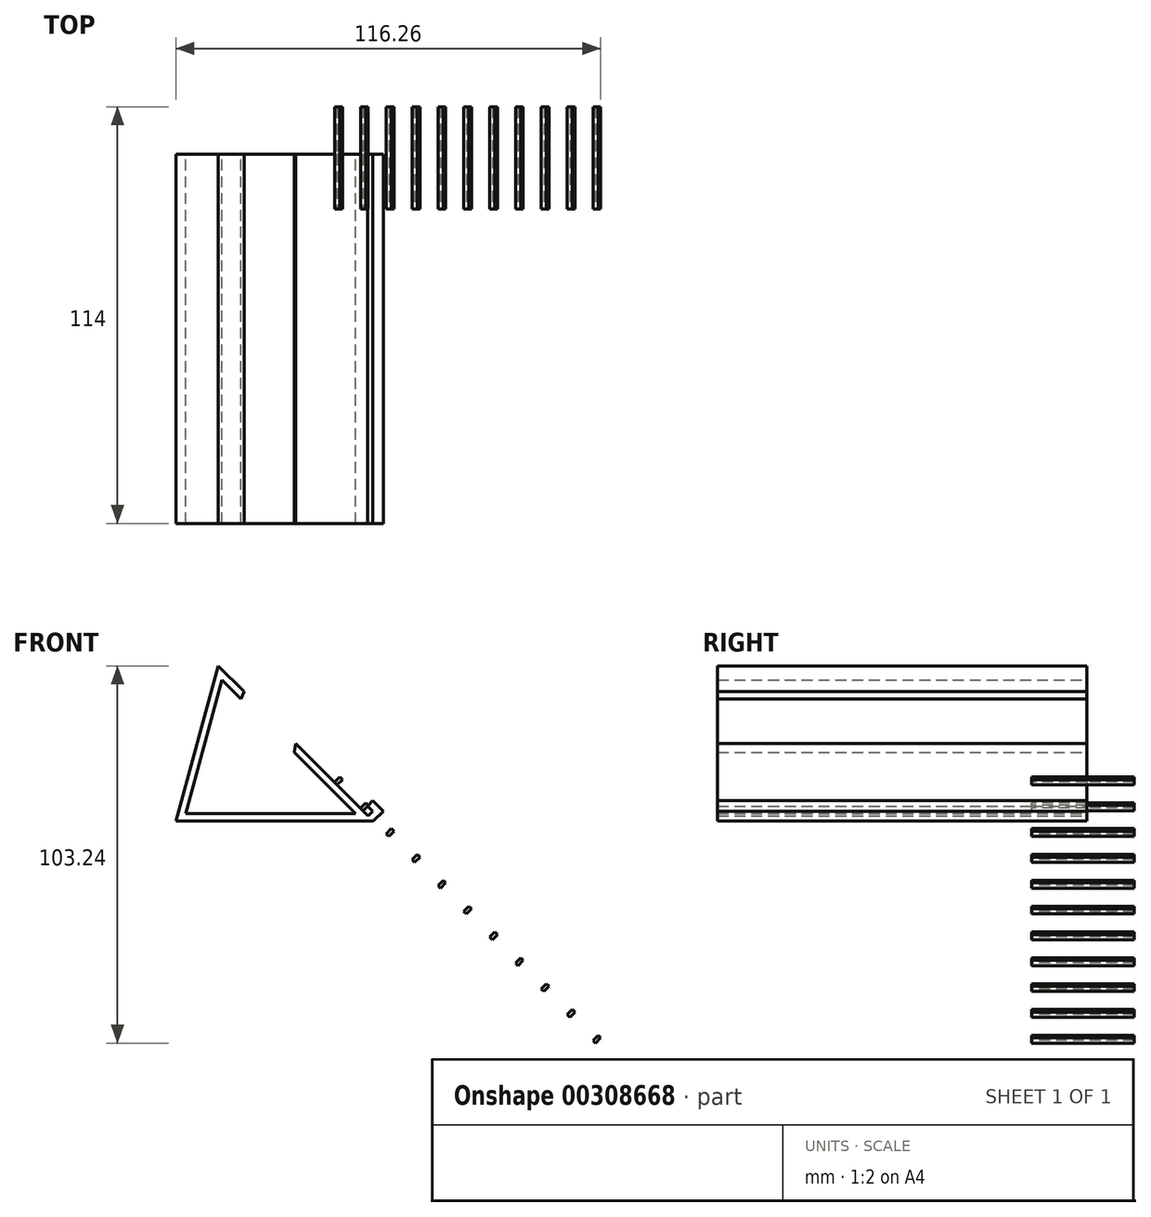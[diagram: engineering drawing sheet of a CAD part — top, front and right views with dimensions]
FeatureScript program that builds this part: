
annotation { "Feature Type Name" : "Feature", "Feature Type Description" : "" }
export const myFeature = defineFeature(function(context is Context, id is Id, definition is map)
    precondition{}
    {
        {
            var Q0;
            Q0=qCreatedBy(makeId("Front.planeOp"),FACE);
            var sketch = newSketch(context, id + "F0", { "sketchPlane" : qUnion([Q0])});
            skLineSegment(sketch, "E0", {"start": v(0, 21.21) * mm, "end": v(21.21, 0) * mm});
            skLineSegment(sketch, "E1", {"start": v(-9.71, 0) * mm, "end": v(21.21, 0) * mm});
            skLineSegment(sketch, "E2", {"start": v(0, 21.21) * mm, "end": v(-14.14, 35.36) * mm});
            skLineSegment(sketch, "E3", {"start": v(-32.82, 0) * mm, "end": v(-9.71, 0) * mm});
            skLineSegment(sketch, "E4", {"start": v(-14.14, 35.36) * mm, "end": v(-21.21, 42.43) * mm});
            skLineSegment(sketch, "E5", {"start": v(-21.21, 42.43) * mm, "end": v(-32.82, 0) * mm});
            skLineSegment(sketch, "E6", {"start": v(-20.2, 38.58) * mm, "end": v(-15.05, 33.44) * mm});
            skLineSegment(sketch, "E7", {"start": v(-15.05, 33.44) * mm, "end": v(-14.14, 35.36) * mm});
            skLineSegment(sketch, "E8", {"start": v(0, 21.21) * mm, "end": v(-0.44, 18.83) * mm});
            skLineSegment(sketch, "E9", {"start": v(-0.44, 18.83) * mm, "end": v(16.38, 2) * mm});
            skLineSegment(sketch, "E10", {"start": v(16.38, 2) * mm, "end": v(-30.2, 2) * mm});
            skLineSegment(sketch, "E11", {"start": v(-30.2, 2) * mm, "end": v(-20.2, 38.58) * mm});
            skLineSegment(sketch, "E12", {"start": v(21.21, 0) * mm, "end": v(23.9, 2.69) * mm});
            skLineSegment(sketch, "E13", {"start": v(23.9, 2.69) * mm, "end": v(21.07, 5.52) * mm});
            skLineSegment(sketch, "E14", {"start": v(21.07, 5.52) * mm, "end": v(19.66, 4.1) * mm});
            skLineSegment(sketch, "E15", {"start": v(19.66, 4.1) * mm, "end": v(21.07, 2.69) * mm});
            skLineSegment(sketch, "E16", {"start": v(21.07, 2.69) * mm, "end": v(19.8, 1.41) * mm});
            skSolve(sketch);
        }
        {
            var Q0;
            {var subQ3=sQuery(id+"F0.wireOp",EDGE,"E1");Q0=makeQuery(id+"F0.imprint","IMPRINT",FACE,{"disambiguationData":[TD([[makeQuery(id+"F0.imprint","IMPRINT",EDGE,{"derivedFrom":subQ3}),1.0]])]});}
            var Q1;
            {var subQ0=sQuery(id+"F0.wireOp",EDGE,"E12");Q1=makeQuery(id+"F0.imprint","IMPRINT",FACE,{"disambiguationData":[TD([[makeQuery(id+"F0.imprint","IMPRINT",EDGE,{"derivedFrom":subQ0}),1.0]])]});}
            extrude(context, id + "F1", {"entities" : qUnion([Q0, Q1]), "depth" : 101 * mm});
        }
        {
            var Q0;
            Q0=makeQuery(id+"F1.opExtrude","SWEPT_FACE",FACE,{"disambiguationData":[OSD([sQuery(id+"F0.wireOp",EDGE,"E0")])]});
            var sketch = newSketch(context, id + "F2", { "sketchPlane" : qUnion([Q0])});
            skLineSegment(sketch, "E17.bottom", {"start": v(13, -101) * mm, "end": v(-15, -101) * mm});
            skLineSegment(sketch, "E17.top", {"start": v(13, -100) * mm, "end": v(-15, -100) * mm});
            skLineSegment(sketch, "E17.left", {"start": v(13, -101) * mm, "end": v(13, -100) * mm});
            skLineSegment(sketch, "E17.right", {"start": v(-15, -101) * mm, "end": v(-15, -100) * mm});
            skLineSegment(sketch, "E18.bottom", {"start": v(13, -91) * mm, "end": v(-15, -91) * mm});
            skLineSegment(sketch, "E18.top", {"start": v(13, -90) * mm, "end": v(-15, -90) * mm});
            skLineSegment(sketch, "E18.left", {"start": v(13, -91) * mm, "end": v(13, -90) * mm});
            skLineSegment(sketch, "E18.right", {"start": v(-15, -91) * mm, "end": v(-15, -90) * mm});
            skLineSegment(sketch, "E19.bottom", {"start": v(13, -81) * mm, "end": v(-15, -81) * mm});
            skLineSegment(sketch, "E19.top", {"start": v(13, -80) * mm, "end": v(-15, -80) * mm});
            skLineSegment(sketch, "E19.left", {"start": v(13, -81) * mm, "end": v(13, -80) * mm});
            skLineSegment(sketch, "E19.right", {"start": v(-15, -81) * mm, "end": v(-15, -80) * mm});
            skLineSegment(sketch, "E20.bottom", {"start": v(13, -71) * mm, "end": v(-15, -71) * mm});
            skLineSegment(sketch, "E20.top", {"start": v(13, -70) * mm, "end": v(-15, -70) * mm});
            skLineSegment(sketch, "E20.left", {"start": v(13, -71) * mm, "end": v(13, -70) * mm});
            skLineSegment(sketch, "E20.right", {"start": v(-15, -71) * mm, "end": v(-15, -70) * mm});
            skLineSegment(sketch, "E21.bottom", {"start": v(13, -61) * mm, "end": v(-15, -61) * mm});
            skLineSegment(sketch, "E21.top", {"start": v(13, -60) * mm, "end": v(-15, -60) * mm});
            skLineSegment(sketch, "E21.left", {"start": v(13, -61) * mm, "end": v(13, -60) * mm});
            skLineSegment(sketch, "E21.right", {"start": v(-15, -61) * mm, "end": v(-15, -60) * mm});
            skLineSegment(sketch, "E22.bottom", {"start": v(13, -51) * mm, "end": v(-15, -51) * mm});
            skLineSegment(sketch, "E22.top", {"start": v(13, -50) * mm, "end": v(-15, -50) * mm});
            skLineSegment(sketch, "E22.left", {"start": v(13, -51) * mm, "end": v(13, -50) * mm});
            skLineSegment(sketch, "E22.right", {"start": v(-15, -51) * mm, "end": v(-15, -50) * mm});
            skLineSegment(sketch, "E23.bottom", {"start": v(13, -41) * mm, "end": v(-15, -41) * mm});
            skLineSegment(sketch, "E23.top", {"start": v(13, -40) * mm, "end": v(-15, -40) * mm});
            skLineSegment(sketch, "E23.left", {"start": v(13, -41) * mm, "end": v(13, -40) * mm});
            skLineSegment(sketch, "E23.right", {"start": v(-15, -41) * mm, "end": v(-15, -40) * mm});
            skLineSegment(sketch, "E24.bottom", {"start": v(13, -31) * mm, "end": v(-15, -31) * mm});
            skLineSegment(sketch, "E24.top", {"start": v(13, -30) * mm, "end": v(-15, -30) * mm});
            skLineSegment(sketch, "E24.left", {"start": v(13, -31) * mm, "end": v(13, -30) * mm});
            skLineSegment(sketch, "E24.right", {"start": v(-15, -31) * mm, "end": v(-15, -30) * mm});
            skLineSegment(sketch, "E25.bottom", {"start": v(13, -21) * mm, "end": v(-15, -21) * mm});
            skLineSegment(sketch, "E25.top", {"start": v(13, -20) * mm, "end": v(-15, -20) * mm});
            skLineSegment(sketch, "E25.left", {"start": v(13, -21) * mm, "end": v(13, -20) * mm});
            skLineSegment(sketch, "E25.right", {"start": v(-15, -21) * mm, "end": v(-15, -20) * mm});
            skLineSegment(sketch, "E26.bottom", {"start": v(13, -1) * mm, "end": v(-15, -1) * mm});
            skLineSegment(sketch, "E26.top", {"start": v(13, 0) * mm, "end": v(-15, 0) * mm});
            skLineSegment(sketch, "E26.left", {"start": v(13, -1) * mm, "end": v(13, 0) * mm});
            skLineSegment(sketch, "E26.right", {"start": v(-15, -1) * mm, "end": v(-15, 0) * mm});
            skLineSegment(sketch, "E27.bottom", {"start": v(13, -11) * mm, "end": v(-15, -11) * mm});
            skLineSegment(sketch, "E27.top", {"start": v(13, -10) * mm, "end": v(-15, -10) * mm});
            skLineSegment(sketch, "E27.left", {"start": v(13, -11) * mm, "end": v(13, -10) * mm});
            skLineSegment(sketch, "E27.right", {"start": v(-15, -11) * mm, "end": v(-15, -10) * mm});
            skSolve(sketch);
        }
        {
            var Q0;
            Q0 = qSketchRegion(id + "F2", true);
            extrude(context, id + "F3", {"entities" : qUnion([Q0]), "operationType" : NewBodyOperationType.ADD, "depth" : 2 * mm});
        }
    });
